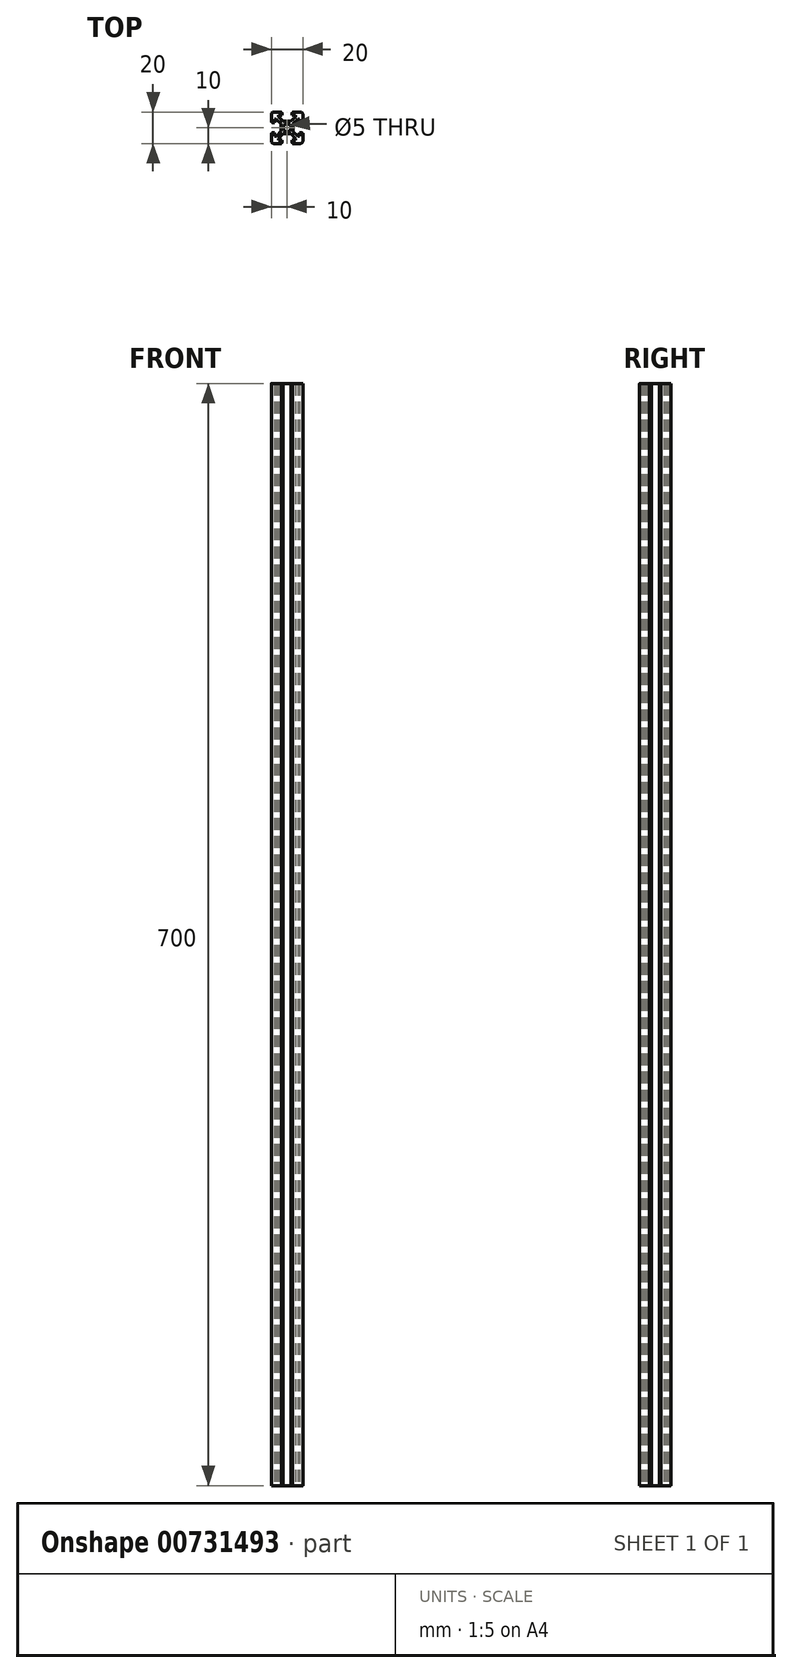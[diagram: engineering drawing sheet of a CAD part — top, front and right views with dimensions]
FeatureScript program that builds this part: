
annotation { "Feature Type Name" : "Feature", "Feature Type Description" : "" }
export const myFeature = defineFeature(function(context is Context, id is Id, definition is map)
    precondition{}
    {
        {
            var Q0;
            Q0=qCreatedBy(makeId("Top.planeOp"),FACE);
            var sketch = newSketch(context, id + "F0", { "sketchPlane" : qUnion([Q0])});
            skLineSegment(sketch, "E0.bottom", {"start": v(-8.5, 10) * mm, "end": v(-3.6, 10) * mm});
            skLineSegment(sketch, "E0.top", {"start": v(-8.5, -10) * mm, "end": v(-3.6, -10) * mm});
            skLineSegment(sketch, "E0.left", {"start": v(-10, 8.5) * mm, "end": v(-10, 3.6) * mm});
            skLineSegment(sketch, "E0.right", {"start": v(10, 8.5) * mm, "end": v(10, 3.6) * mm});
            skArc(sketch, "E1.filletArc", {"start": v(-8.5, 10) * mm, "mid": v(-9.56, 9.56) * mm, "end": v(-10, 8.5) * mm});
            skArc(sketch, "E2.filletArc", {"start": v(10, 8.5) * mm, "mid": v(9.56, 9.56) * mm, "end": v(8.5, 10) * mm});
            skArc(sketch, "E3.filletArc", {"start": v(8.5, -10) * mm, "mid": v(9.56, -9.56) * mm, "end": v(10, -8.5) * mm});
            skArc(sketch, "E4.filletArc", {"start": v(-10, -8.5) * mm, "mid": v(-9.56, -9.56) * mm, "end": v(-8.5, -10) * mm});
            skLineSegment(sketch, "E5.bottom", {"start": v(-5.5, 8) * mm, "end": v(-3.1, 8) * mm});
            skLineSegment(sketch, "E5.top", {"start": v(-5.5, -8) * mm, "end": v(-3.1, -8) * mm});
            skLineSegment(sketch, "E5.left", {"start": v(-8, 5.5) * mm, "end": v(-8, 3.1) * mm});
            skLineSegment(sketch, "E5.right", {"start": v(8, 5.5) * mm, "end": v(8, 3.1) * mm});
            skCircle(sketch, "E6", {"center": v(0, 0) * mm, "radius": 2.5 * mm});
            skLineSegment(sketch, "E7.right", {"start": v(5.5, -8) * mm, "end": v(5.5, -6.91) * mm});
            skLineSegment(sketch, "E8.top", {"start": v(8, 5.5) * mm, "end": v(7.01, 5.5) * mm});
            skLineSegment(sketch, "E9.bottom", {"start": v(-2.59, 4) * mm, "end": v(2.29, 4) * mm});
            skLineSegment(sketch, "E9.top", {"start": v(-2.67, -3.8) * mm, "end": v(2.39, -3.8) * mm});
            skLineSegment(sketch, "E9.left", {"start": v(-4, 2.59) * mm, "end": v(-4, -2.29) * mm});
            skLineSegment(sketch, "E9.right", {"start": v(3.8, 2.67) * mm, "end": v(3.8, -2.39) * mm});
            skLineSegment(sketch, "E10.trimOffspring", {"start": v(8, -5.5) * mm, "end": v(6.91, -5.5) * mm});
            skLineSegment(sketch, "E11.trimOffspring", {"start": v(-5.5, -8) * mm, "end": v(-5.5, -7.01) * mm});
            skLineSegment(sketch, "E12.left", {"start": v(-3.1, 9.5) * mm, "end": v(-3.1, 8) * mm});
            skLineSegment(sketch, "E12.right", {"start": v(3.1, 9.5) * mm, "end": v(3.1, 8) * mm});
            skLineSegment(sketch, "E13.trimOffspring", {"start": v(3.6, 10) * mm, "end": v(8.5, 10) * mm});
            skLineSegment(sketch, "E14.trimOffspring", {"start": v(3.1, 8) * mm, "end": v(5.5, 8) * mm});
            skLineSegment(sketch, "E15.left", {"start": v(-3.1, -9.5) * mm, "end": v(-3.1, -8) * mm});
            skLineSegment(sketch, "E15.right", {"start": v(3.1, -9.5) * mm, "end": v(3.1, -8) * mm});
            skLineSegment(sketch, "E16.trimOffspring", {"start": v(3.1, -8) * mm, "end": v(5.5, -8) * mm});
            skLineSegment(sketch, "E17.trimOffspring", {"start": v(3.6, -10) * mm, "end": v(8.5, -10) * mm});
            skLineSegment(sketch, "E18.bottom", {"start": v(9.5, 3.1) * mm, "end": v(8, 3.1) * mm});
            skLineSegment(sketch, "E18.top", {"start": v(9.5, -3.1) * mm, "end": v(8, -3.1) * mm});
            skLineSegment(sketch, "E19.trimOffspring", {"start": v(8, -3.1) * mm, "end": v(8, -5.5) * mm});
            skLineSegment(sketch, "E20.trimOffspring", {"start": v(10, -3.6) * mm, "end": v(10, -8.5) * mm});
            skLineSegment(sketch, "E21.bottom", {"start": v(-9.5, 3.1) * mm, "end": v(-8, 3.1) * mm});
            skLineSegment(sketch, "E21.top", {"start": v(-9.5, -3.1) * mm, "end": v(-8, -3.1) * mm});
            skLineSegment(sketch, "E22.trimOffspring", {"start": v(-10, -3.6) * mm, "end": v(-10, -8.5) * mm});
            skLineSegment(sketch, "E23.trimOffspring", {"start": v(-8, -3.1) * mm, "end": v(-8, -5.5) * mm});
            skLineSegment(sketch, "E24.top", {"start": v(-3.6, -9.5) * mm, "end": v(-3.1, -9.5) * mm});
            skLineSegment(sketch, "E24.left", {"start": v(-3.6, -10) * mm, "end": v(-3.6, -9.5) * mm});
            skLineSegment(sketch, "E24.right", {"start": v(3.6, -10) * mm, "end": v(3.6, -9.5) * mm});
            skLineSegment(sketch, "E25.trimOffspring", {"start": v(3.1, -9.5) * mm, "end": v(3.6, -9.5) * mm});
            skLineSegment(sketch, "E26.trimOffspring", {"start": v(-6.91, 5.5) * mm, "end": v(-8, 5.5) * mm});
            skLineSegment(sketch, "E27.trimOffspring", {"start": v(-5.5, 6.91) * mm, "end": v(-5.5, 8) * mm});
            skLineSegment(sketch, "E28.trimOffspring", {"start": v(-6.83, -5.5) * mm, "end": v(-8, -5.5) * mm});
            skLineSegment(sketch, "E29.trimOffspring", {"start": v(5.5, 6.83) * mm, "end": v(5.5, 8) * mm});
            skLineSegment(sketch, "E30.bottom", {"start": v(-10, 3.6) * mm, "end": v(-9.5, 3.6) * mm});
            skLineSegment(sketch, "E30.top", {"start": v(-10, -3.6) * mm, "end": v(-9.5, -3.6) * mm});
            skLineSegment(sketch, "E30.right", {"start": v(-9.5, 3.6) * mm, "end": v(-9.5, 3.1) * mm});
            skLineSegment(sketch, "E31.trimOffspring", {"start": v(-9.5, -3.1) * mm, "end": v(-9.5, -3.6) * mm});
            skLineSegment(sketch, "E32.top", {"start": v(-3.6, 9.5) * mm, "end": v(-3.1, 9.5) * mm});
            skLineSegment(sketch, "E32.left", {"start": v(-3.6, 10) * mm, "end": v(-3.6, 9.5) * mm});
            skLineSegment(sketch, "E32.right", {"start": v(3.6, 10) * mm, "end": v(3.6, 9.5) * mm});
            skLineSegment(sketch, "E33.trimOffspring", {"start": v(3.1, 9.5) * mm, "end": v(3.6, 9.5) * mm});
            skLineSegment(sketch, "E34", {"start": v(9.5, 3.1) * mm, "end": v(9.5, 3.6) * mm});
            skLineSegment(sketch, "E35", {"start": v(9.5, 3.6) * mm, "end": v(10, 3.6) * mm});
            skLineSegment(sketch, "E36", {"start": v(9.5, -3.1) * mm, "end": v(9.5, -3.6) * mm});
            skLineSegment(sketch, "E37", {"start": v(9.5, -3.6) * mm, "end": v(10, -3.6) * mm});
            skLineSegment(sketch, "E38.0", {"start": v(5.5, 6.83) * mm, "end": v(2.29, 4) * mm});
            skLineSegment(sketch, "E39.0", {"start": v(7.01, 5.5) * mm, "end": v(3.8, 2.67) * mm});
            skLineSegment(sketch, "E40.0", {"start": v(-6.91, 5.5) * mm, "end": v(-4, 2.59) * mm});
            skLineSegment(sketch, "E41.0", {"start": v(-5.5, 6.91) * mm, "end": v(-2.59, 4) * mm});
            skLineSegment(sketch, "E42.0", {"start": v(-5.5, -7.01) * mm, "end": v(-2.67, -3.8) * mm});
            skLineSegment(sketch, "E43.0", {"start": v(-6.83, -5.5) * mm, "end": v(-4, -2.29) * mm});
            skLineSegment(sketch, "E44.0", {"start": v(6.91, -5.5) * mm, "end": v(3.8, -2.39) * mm});
            skLineSegment(sketch, "E45.0", {"start": v(5.5, -6.91) * mm, "end": v(2.39, -3.8) * mm});
            skSolve(sketch);
        }
        {
            var Q0;
            Q0=qSketchRegion(id+"F0",true);
            extrude(context, id + "F1", {"entities" : qUnion([Q0]), "depth" : 700 * mm, "offsetDistance" : 25 * mm});
        }
    });
